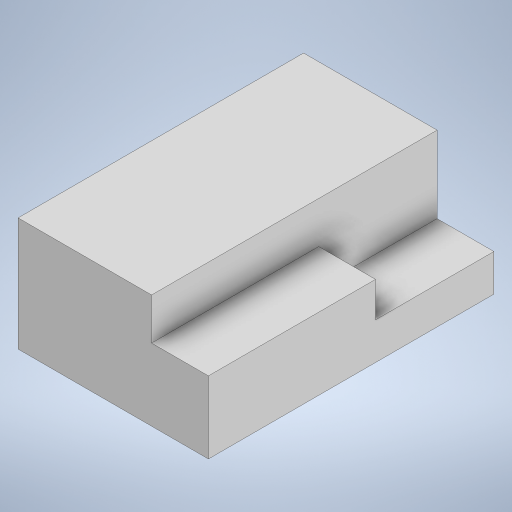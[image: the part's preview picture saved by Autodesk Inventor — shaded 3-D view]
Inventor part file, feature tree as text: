
AUTODESK INVENTOR PART (.ipt)
format: ipt  version: 2024 (Build 280153000, 153)  size: 214,016 bytes
history: native  units: in
note: dims shown in document units (in); Inventor stores cm internally (conversion verified against a paired STEP export)
features: extrude x3, sketch x3, projected_geometry x2
ambient origin geometry x8: Origin, YZ Plane, XZ Plane, XY Plane, X Axis, Y Axis, Z Axis, Center Point
bodies: Solid1 (feature_tree)
feature tree (8):
  extrude  "Extrusion1"  Depth=1.5827in
  extrude  "Extrusion2"  Depth=0.4724in
  extrude  "Extrusion3"  TaperAngle=0.0deg  [1 undecoded]
  sketch  "Sketch1"  dims[d0=2.374in d1=1.5827in]
  sketch  "Sketch2"  dims[d2=0.9449in d3=0.0in d4=0.4724in]
  projected_geometry  "Projected Loop1"
  sketch  "Sketch3"  dims[d5=0.3465in d6=0.0in d7=0.0in d8=0.9843in d9=0.2913in d10=1.0in d11=0.0in]
  projected_geometry  "Projected Loop2"
note: 1 required parameter value undecoded (feature->parameter linkage not recoverable at this tier; creation-order binding heuristic only, values carry confidence <= 0.55)
